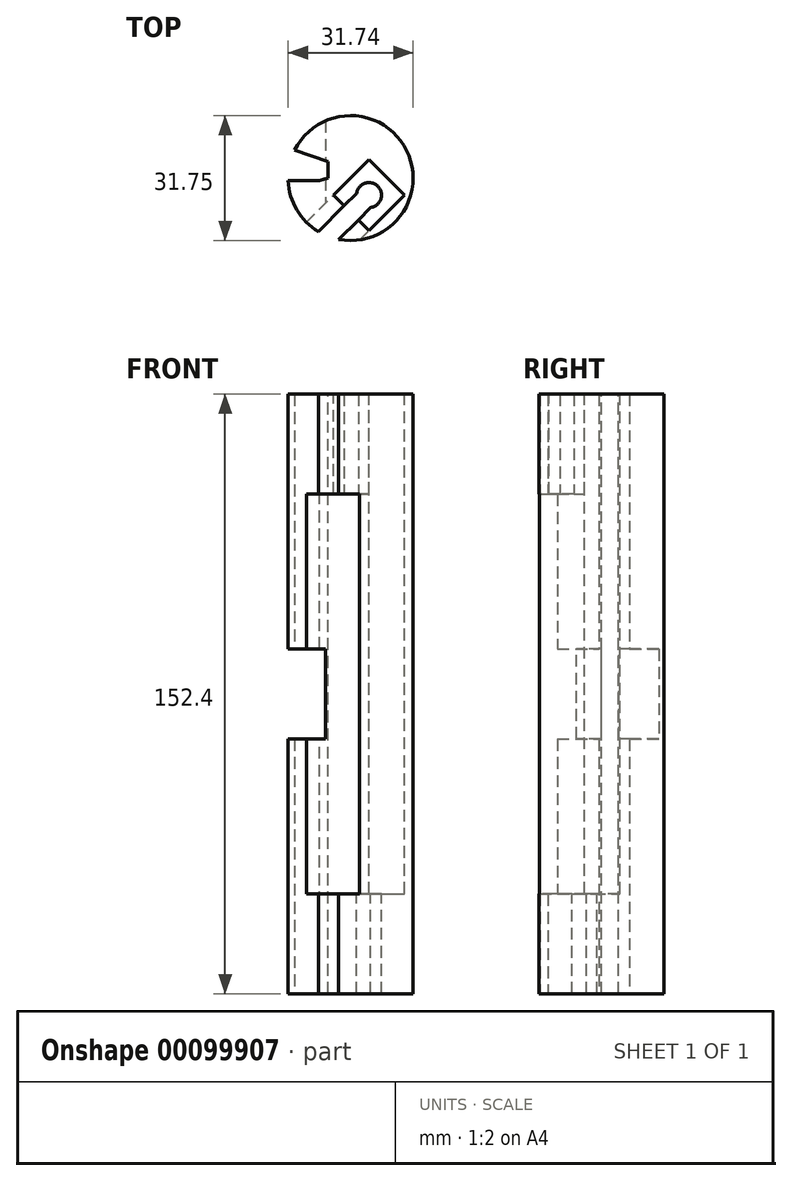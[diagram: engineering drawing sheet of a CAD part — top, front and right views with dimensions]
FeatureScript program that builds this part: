
annotation { "Feature Type Name" : "Feature", "Feature Type Description" : "" }
export const myFeature = defineFeature(function(context is Context, id is Id, definition is map)
    precondition{}
    {
        {
            var Q0;
            Q0=qCreatedBy(makeId("Top.planeOp"),FACE);
            var sketch = newSketch(context, id + "F0", { "sketchPlane" : qUnion([Q0])});
            skCircle(sketch, "E0", {"center": v(0, 0) * mm, "radius": 15.88 * mm});
            skSolve(sketch);
        }
        {
            var Q0;
            Q0 = qSketchRegion(id + "F0", true);
            extrude(context, id + "F1", {"entities" : qUnion([Q0]), "depth" : 152.4 * mm});
        }
        {
            var Q0;
            Q0=makeQuery(id+"F1.opExtrude","CAP_FACE",FACE,{"disambiguationData":[OSD([sQuery(id+"F0.wireOp",EDGE,"E0")])],"isStart":false});
            var sketch = newSketch(context, id + "F2", { "sketchPlane" : qUnion([Q0])});
            skLineSegment(sketch, "E1.bottom", {"start": v(-4.32, -4.32) * mm, "end": v(4.66, 4.66) * mm});
            skLineSegment(sketch, "E1.top", {"start": v(4.66, -13.3) * mm, "end": v(13.64, -4.32) * mm});
            skLineSegment(sketch, "E1.left", {"start": v(-4.32, -4.32) * mm, "end": v(4.66, -13.3) * mm});
            skLineSegment(sketch, "E1.right", {"start": v(4.66, 4.66) * mm, "end": v(13.64, -4.32) * mm});
            skLineSegment(sketch, "E2", {"start": v(0, 15.88) * mm, "end": v(0, -15.88) * mm, "construction": true});
            skLineSegment(sketch, "E3", {"start": v(-4.32, -4.32) * mm, "end": v(13.64, -4.32) * mm, "construction": true});
            skSolve(sketch);
        }
        {
            var Q0;
            Q0 = qSketchRegion(id + "F2", true);
            extrude(context, id + "F3", {"entities" : qUnion([Q0]), "operationType" : NewBodyOperationType.REMOVE, "oppositeDirection" : true, "depth" : 127 * mm});
        }
        {
            var Q0;
            Q0=makeQuery(id+"F1.opExtrude","CAP_FACE",FACE,{"disambiguationData":[OSD([sQuery(id+"F0.wireOp",EDGE,"E0")])],"isStart":false});
            var sketch = newSketch(context, id + "F4", { "sketchPlane" : qUnion([Q0])});
            skLineSegment(sketch, "E4", {"start": v(4.66, 4.66) * mm, "end": v(4.66, -13.3) * mm, "construction": true});
            skLineSegment(sketch, "E5", {"start": v(-4.32, -4.32) * mm, "end": v(13.64, -4.32) * mm, "construction": true});
            skPoint(sketch, "E6", {"position": v(4.66, -4.32) * mm});
            skCircle(sketch, "E7", {"center": v(4.66, -4.32) * mm, "radius": 3.18 * mm});
            skSolve(sketch);
        }
        {
            var Q0;
            Q0 = qSketchRegion(id + "F4", true);
            extrude(context, id + "F5", {"entities" : qUnion([Q0]), "operationType" : NewBodyOperationType.REMOVE, "oppositeDirection" : true, "depth" : 152.4 * mm});
        }
        {
            var Q0;
            Q0=makeQuery(id+"F1.opExtrude","CAP_FACE",FACE,{"disambiguationData":[OSD([sQuery(id+"F0.wireOp",EDGE,"E0")])],"isStart":false});
            cPlane(context, id + "F6", {"entities" : qUnion([Q0]), "cplaneType" : CPlaneType.OFFSET, "offset" : 25.4 * mm, "oppositeDirection" : true, "width" : 152.4 * mm, "height" : 152.4 * mm});
        }
        {
            var Q0;
            Q0=qCreatedBy(id+"F6.planeOp",FACE);
            var sketch = newSketch(context, id + "F7", { "sketchPlane" : qUnion([Q0])});
            skLineSegment(sketch, "E8.bottom", {"start": v(0, 0) * mm, "end": v(8.98, -8.98) * mm});
            skLineSegment(sketch, "E8.top", {"start": v(-17.96, -17.96) * mm, "end": v(-8.98, -26.94) * mm});
            skLineSegment(sketch, "E8.left", {"start": v(-17.96, -17.96) * mm, "end": v(0, 0) * mm});
            skLineSegment(sketch, "E8.right", {"start": v(-8.98, -26.94) * mm, "end": v(8.98, -8.98) * mm});
            skSolve(sketch);
        }
        {
            var Q0;
            Q0 = qSketchRegion(id + "F7", true);
            extrude(context, id + "F8", {"entities" : qUnion([Q0]), "operationType" : NewBodyOperationType.REMOVE, "oppositeDirection" : true, "depth" : 101.6 * mm});
        }
        {
            var Q0;
            Q0=makeQuery(id+"F8.boolean.opBoolean","MERGE",FACE,{"derivedFrom":[makeQuery(id+"F3.boolean.opBoolean","COPY",FACE,{"derivedFrom":makeQuery(id+"F3.opExtrude","CAP_FACE",FACE,{"disambiguationData":[OSD([sQuery(id+"F2.wireOp",EDGE,"E1.bottom"),sQuery(id+"F2.wireOp",EDGE,"E1.top"),sQuery(id+"F2.wireOp",EDGE,"E1.left"),sQuery(id+"F2.wireOp",EDGE,"E1.right")])],"isStart":false})}),makeQuery(id+"F8.opExtrude","CAP_FACE",FACE,{"disambiguationData":[OSD([sQuery(id+"F7.wireOp",EDGE,"E8.bottom"),sQuery(id+"F7.wireOp",EDGE,"E8.top"),sQuery(id+"F7.wireOp",EDGE,"E8.left"),sQuery(id+"F7.wireOp",EDGE,"E8.right")])],"isStart":false})]});
            var sketch = newSketch(context, id + "F9", { "sketchPlane" : qUnion([Q0])});
            skLineSegment(sketch, "E9.bottom", {"start": v(5.11, -7.46) * mm, "end": v(1.52, -3.87) * mm});
            skLineSegment(sketch, "E9.top", {"start": v(-6.87, -19.44) * mm, "end": v(-10.46, -15.85) * mm});
            skLineSegment(sketch, "E9.left", {"start": v(1.52, -3.87) * mm, "end": v(-10.46, -15.85) * mm});
            skLineSegment(sketch, "E9.right", {"start": v(5.11, -7.46) * mm, "end": v(-6.87, -19.44) * mm});
            skSolve(sketch);
        }
        {
            var Q0;
            Q0 = qSketchRegion(id + "F9", true);
            extrude(context, id + "F10", {"entities" : qUnion([Q0]), "operationType" : NewBodyOperationType.REMOVE, "endBound" : BoundingType.THROUGH_ALL, "oppositeDirection" : true, "depth" : 25.4 * mm, "hasSecondDirection" : true, "secondDirectionBound" : SecondDirectionBoundingType.THROUGH_ALL, "secondDirectionOppositeDirection" : false, "secondDirectionDepth" : 25.4 * mm});
        }
        {
            var Q0;
            Q0=makeQuery(id+"F1.opExtrude","CAP_FACE",FACE,{"disambiguationData":[OSD([sQuery(id+"F0.wireOp",EDGE,"E0")])],"isStart":false});
            var sketch = newSketch(context, id + "F11", { "sketchPlane" : qUnion([Q0])});
            skPoint(sketch, "E10.middle", {"position": v(-15.88, 0) * mm});
            skLineSegment(sketch, "E11", {"start": v(-27, 10.12) * mm, "end": v(-23.28, 10.12) * mm});
            skLineSegment(sketch, "E12", {"start": v(-23.28, 10.12) * mm, "end": v(-5.76, 4.24) * mm});
            skLineSegment(sketch, "E13", {"start": v(-5.76, 4.24) * mm, "end": v(-5.76, 0) * mm});
            skLineSegment(sketch, "E14", {"start": v(-5.76, 0) * mm, "end": v(-7.94, -0.68) * mm});
            skLineSegment(sketch, "E15", {"start": v(-7.94, -0.68) * mm, "end": v(-27, -0.68) * mm});
            skLineSegment(sketch, "E16", {"start": v(-27, -0.68) * mm, "end": v(-27, 10.12) * mm});
            skSolve(sketch);
        }
        {
            var Q0;
            Q0 = qSketchRegion(id + "F11", true);
            extrude(context, id + "F12", {"entities" : qUnion([Q0]), "operationType" : NewBodyOperationType.REMOVE, "endBound" : BoundingType.THROUGH_ALL, "oppositeDirection" : true, "depth" : 25.4 * mm});
        }
        {
            var Q0;
            Q0=qCreatedBy(makeId("Front.planeOp"),FACE);
            var sketch = newSketch(context, id + "F13", { "sketchPlane" : qUnion([Q0])});
            skLineSegment(sketch, "E17", {"start": v(0, 0) * mm, "end": v(0, 76.2) * mm, "construction": true});
            skLineSegment(sketch, "E18", {"start": v(0, 76.2) * mm, "end": v(-15.88, 76.2) * mm, "construction": true});
            skLineSegment(sketch, "E19.bottom", {"start": v(-25.4, 64.77) * mm, "end": v(-6.35, 64.77) * mm});
            skLineSegment(sketch, "E19.top", {"start": v(-25.4, 87.63) * mm, "end": v(-6.35, 87.63) * mm});
            skLineSegment(sketch, "E19.left", {"start": v(-25.4, 64.77) * mm, "end": v(-25.4, 87.63) * mm});
            skLineSegment(sketch, "E19.right", {"start": v(-6.35, 64.77) * mm, "end": v(-6.35, 87.63) * mm});
            skPoint(sketch, "E19.middle", {"position": v(-15.88, 76.2) * mm});
            skSolve(sketch);
        }
        {
            var Q0;
            Q0 = qSketchRegion(id + "F13", true);
            extrude(context, id + "F14", {"entities" : qUnion([Q0]), "operationType" : NewBodyOperationType.REMOVE, "endBound" : BoundingType.THROUGH_ALL, "oppositeDirection" : true, "depth" : 25.4 * mm, "hasSecondDirection" : true, "secondDirectionBound" : SecondDirectionBoundingType.THROUGH_ALL, "secondDirectionOppositeDirection" : false, "secondDirectionDepth" : 25.4 * mm});
        }
        {
            var Q0;
            Q0=qCreatedBy(makeId("Top.planeOp"),FACE);
            cPlane(context, id + "F15", {"entities" : qUnion([Q0]), "cplaneType" : CPlaneType.OFFSET, "offset" : 76.2 * mm, "width" : 152.4 * mm, "height" : 152.4 * mm});
        }
    });
